# Revit family: Electronics_Conferencing-Cameras_Biamp_Vidi_4K_100_150___
name_source: partatom
category: Communication Devices
units: mm (PartAtom-declared; Revit-internal decimal feet)

## family parameters
Cut with Voids When Loaded = No
Host = Face
Maintain Annotation Orientation = No
OmniClass Number = 23.85.10.14.11
OmniClass Title = Cameras
Part Type = Normal
Room Calculation Point = No
Round Connector Dimension = Use Diameter
Shared = No

## types (2) — shared parameters
Apparent Load = 0 VA
Backlight Compensation = Supported
Bit Depth = 24-bit
Compliance = CE Marked (Europe), RoHS Directive (Europe)
Connector = USB 3.0 Type-B
Connector Description = USB
Connector Video = USB
Default Elevation = 48 "
Depth = 1.3 "
Digital Noise Reduction = 2D and 3D
Field Of View Horizontal = 120.00°
Field Of View Vertical = 120.00°
Field-Of-View Diagonal = 120°
Focus = 2.8mm
Height = 1.7 "
Housing Material = Biamp - Plastic - Black
Image sensor = 8MP, 1/2.5”, CMOS, progressive scan
Manufacturer = Biamp
Max Power Consumption = 0 W
Number of Poles = 1
Power Factor = 1
Product Documentation Link = https://downloads.biamp.com
Product Page URL = https://www.biamp.com
Product data url = https://www.bimobject.com
Sample Rate = 48 kHz
Signal Noise Ratio = > 55dB
Supported Resolutions = Up to 3840 x 2160p (30fps)
Temperature Range = 50-86° F (10-30° C)
URL = https://www.biamp.com
Voltage = 0 V
Weight = 0.70 lbf
White Balance = Auto
Width = 7.6 "
Zoom = 3x Digital

## per-type parameters (varying)
| type | Description | Positioning |
| Vidi 100 | Vidi™ 100 4K Conferencing Camera | Electronic Pan/Tilt/Zoom |
| Vidi 150 | Vidi™ 150 4K Conferencing Camera | Autoframing capability/Electronic Pan/Tilt/Zoom |

note: column(s) folded — value = type name in every type: Model

## geometry (parser evidence)
native form markers: Sweep x3
no freeform markers — native parametric forms only
